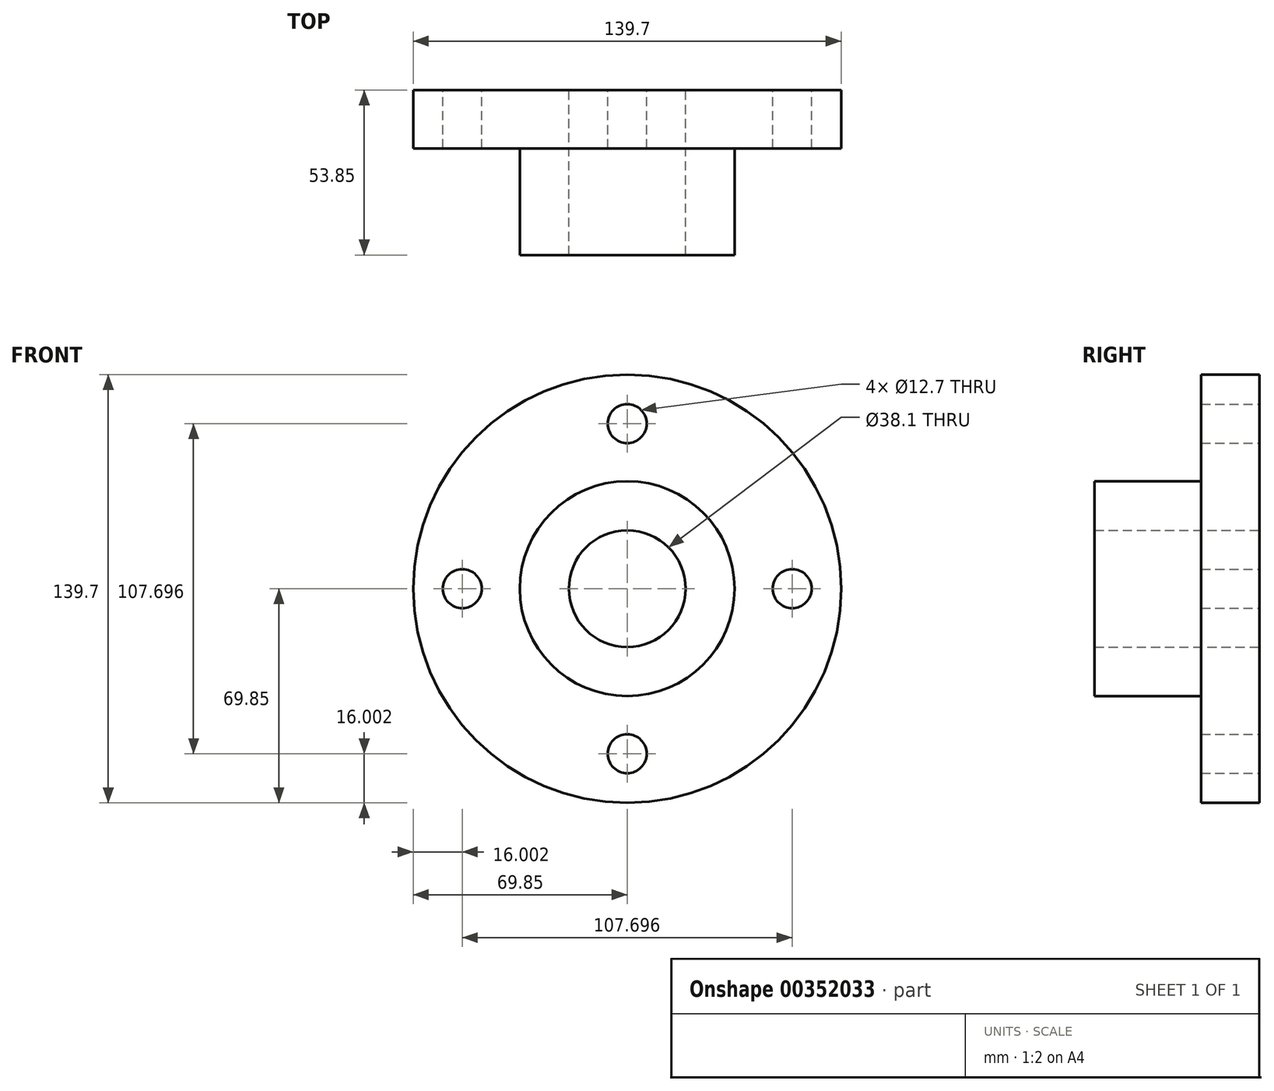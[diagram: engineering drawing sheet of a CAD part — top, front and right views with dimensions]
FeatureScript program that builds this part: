
annotation { "Feature Type Name" : "Feature", "Feature Type Description" : "" }
export const myFeature = defineFeature(function(context is Context, id is Id, definition is map)
    precondition{}
    {
        {
            var Q0;
            Q0=qCreatedBy(makeId("Front.planeOp"),FACE);
            var sketch = newSketch(context, id + "F0", { "sketchPlane" : qUnion([Q0])});
            skCircle(sketch, "E0", {"center": v(0, 0) * mm, "radius": 19.05 * mm});
            skCircle(sketch, "E1", {"center": v(0, 0) * mm, "radius": 35.05 * mm});
            skCircle(sketch, "E2", {"center": v(0, 0) * mm, "radius": 53.85 * mm});
            skCircle(sketch, "E3", {"center": v(0, 0) * mm, "radius": 69.85 * mm});
            skCircle(sketch, "E4", {"center": v(0, 53.85) * mm, "radius": 6.35 * mm});
            skCircle(sketch, "E5", {"center": v(-53.85, 0) * mm, "radius": 6.35 * mm});
            skCircle(sketch, "E6", {"center": v(0, -53.85) * mm, "radius": 6.35 * mm});
            skCircle(sketch, "E7", {"center": v(53.85, 0) * mm, "radius": 6.35 * mm});
            skSolve(sketch);
        }
        {
            var Q0;
            Q0=makeQuery(id+"F0.imprint","IMPRINT",FACE,{"disambiguationData":[TD([[makeQuery(id+"F0.imprint","IMPRINT",EDGE,{"derivedFrom":sQuery(id+"F0.wireOp",EDGE,"E0")}),-1.0]])]});
            extrude(context, id + "F1", {"entities" : qUnion([Q0]), "depth" : 53.85 * mm});
        }
        {
            var Q0;
            Q0=makeQuery(id+"F0.imprint","IMPRINT",FACE,{"disambiguationData":[TD([[makeQuery(id+"F0.imprint","IMPRINT",EDGE,{"derivedFrom":sQuery(id+"F0.wireOp",EDGE,"E3")}),1.0]])]});
            var Q1;
            Q1=makeQuery(id+"F0.imprint","IMPRINT",FACE,{"disambiguationData":[TD([[makeQuery(id+"F0.imprint","IMPRINT",EDGE,{"derivedFrom":sQuery(id+"F0.wireOp",EDGE,"E1")}),-1.0]])]});
            extrude(context, id + "F2", {"entities" : qUnion([Q0, Q1]), "operationType" : NewBodyOperationType.ADD, "depth" : 19.05 * mm});
        }
    });
